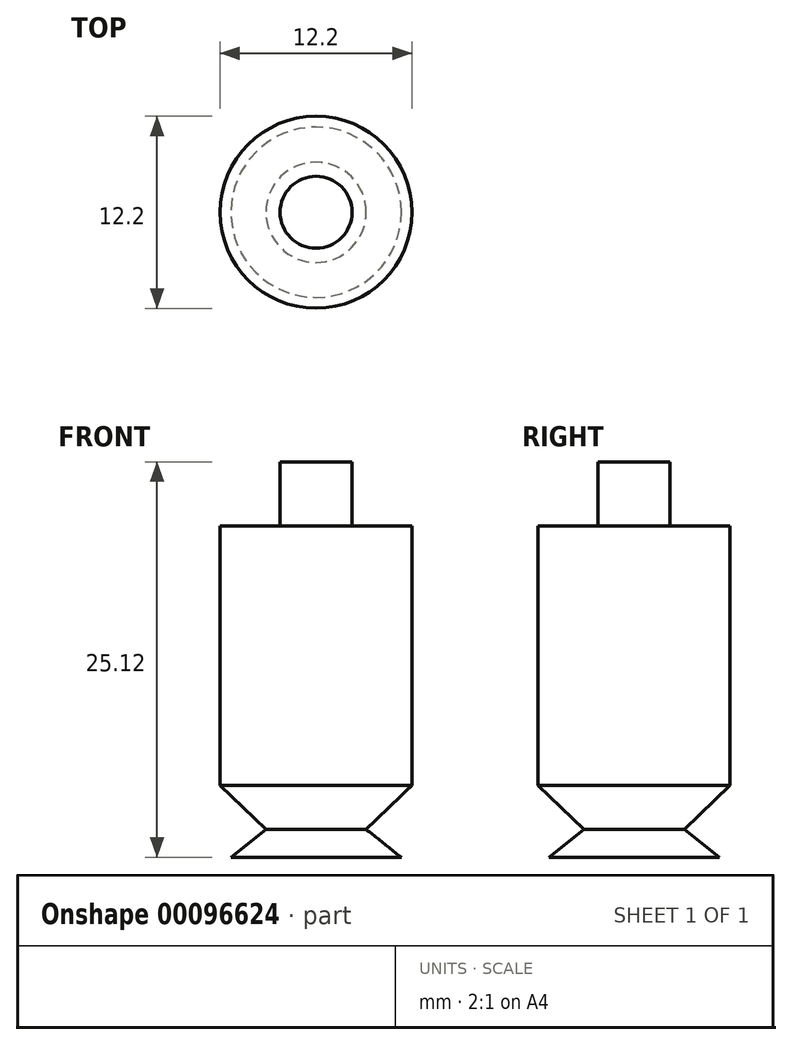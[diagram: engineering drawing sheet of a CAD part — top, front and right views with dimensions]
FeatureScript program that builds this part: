
annotation { "Feature Type Name" : "Feature", "Feature Type Description" : "" }
export const myFeature = defineFeature(function(context is Context, id is Id, definition is map)
    precondition{}
    {
        {
            var Q0;
            Q0=qCreatedBy(makeId("Front.planeOp"),FACE);
            var sketch = newSketch(context, id + "F0", { "sketchPlane" : qUnion([Q0])});
            skLineSegment(sketch, "E0", {"start": v(6.1, 4.57) * mm, "end": v(6.1, 21.06) * mm});
            skLineSegment(sketch, "E1", {"start": v(6.1, 21.06) * mm, "end": v(2.29, 21.06) * mm});
            skLineSegment(sketch, "E2", {"start": v(2.29, 21.06) * mm, "end": v(2.29, 25.12) * mm});
            skLineSegment(sketch, "E3", {"start": v(2.29, 25.12) * mm, "end": v(0, 25.12) * mm});
            skLineSegment(sketch, "E4", {"start": v(0, 25.12) * mm, "end": v(0, 0) * mm});
            skLineSegment(sketch, "E5", {"start": v(5.41, 0) * mm, "end": v(3.18, 1.77) * mm});
            skLineSegment(sketch, "E6", {"start": v(3.18, 1.77) * mm, "end": v(6.1, 4.57) * mm});
            skLineSegment(sketch, "E7", {"start": v(0, 0) * mm, "end": v(5.41, 0) * mm});
            skSolve(sketch);
        }
        {
            var Q0;
            Q0=makeQuery(id+"F0.imprint","IMPRINT",FACE,{"disambiguationData":[TD([[makeQuery(id+"F0.imprint","IMPRINT",EDGE,{"derivedFrom":sQuery(id+"F0.wireOp",EDGE,"zuYLiWgT-2qJT-Agsl-ibZ5-obHifS6ynjOX")}),1.0]])]});
            var Q1;
            Q1=makeQuery(id+"F0.imprint","IMPRINT",FACE,{"disambiguationData":[TD([[makeQuery(id+"F0.imprint","IMPRINT",EDGE,{"derivedFrom":sQuery(id+"F0.wireOp",EDGE,"E0")}),1.0]])]});
            var Q2;
            Q2=sQuery(id+"F0.wireOp",EDGE,"E4");
            revolve(context, id + "F1", {"entities" : qUnion([Q0, Q1]), "axis" : qUnion([Q2]), "revolveType" : RevolveType.FULL});
        }
    });
